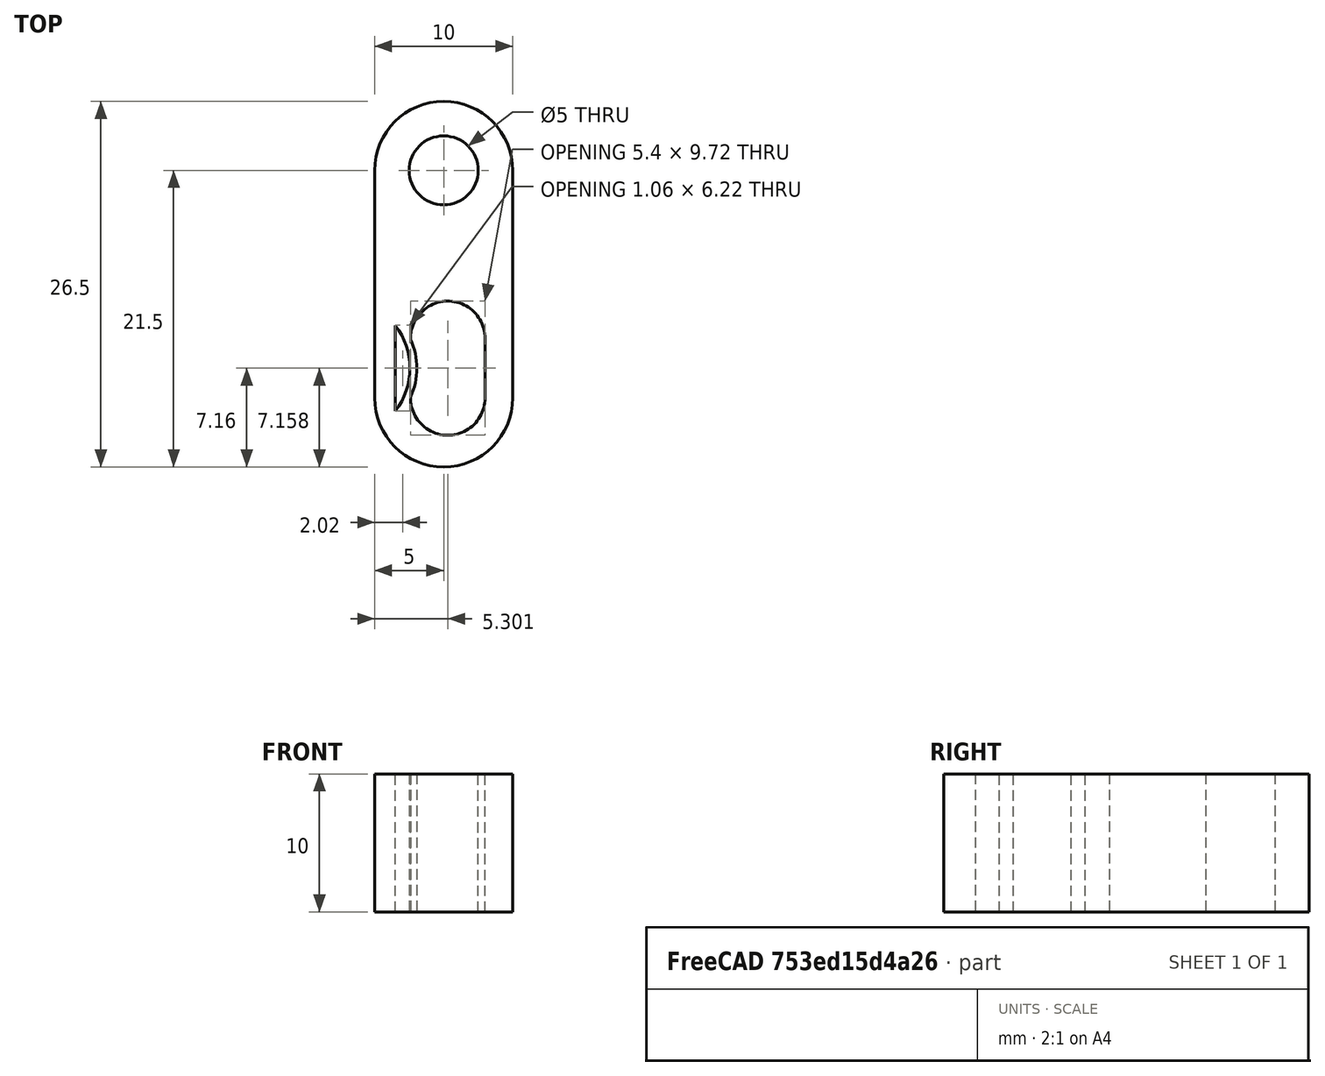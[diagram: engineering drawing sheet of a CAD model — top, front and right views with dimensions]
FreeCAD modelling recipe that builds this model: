
FCSTD DOCUMENT  (FreeCAD 0.22R38467 (Git))
Label: Actuator Arm
objects: Sketcher::SketchObject×2, PartDesign::CoordinateSystem×1, Part::Extrusion×1, App::Part×1
note: 6 computed .brp shape members not serialized (recipe doc carries the construction recipe); baked Part::Feature solids carry a one-line shape summary decoded from their .brp

FEATURE [Sketcher::SketchObject] Sketch001  label="Master Sketch"
  ArcFitTolerance = 1e-06
  FullyConstrained = false
  MakeInternals = false
  sketch-geometry (42):
    g0: Circle CenterX=-4e-16 CenterY=0 CenterZ=0 NormalX=0 NormalY=0 NormalZ=1 AngleXU=0 Radius=50
    g1: LineSegment [constr] StartX=-4e-16 StartY=0 StartZ=0 EndX=-15.4508 EndY=-47.5528 EndZ=0
    g2: LineSegment [constr] StartX=-4e-16 StartY=0 StartZ=0 EndX=15.4508 EndY=-47.5528 EndZ=0
    g3: LineSegment StartX=4.16347 StartY=-17.7687 StartZ=0 EndX=-5.80371 EndY=-32.7572 EndZ=0
    g4: LineSegment StartX=-6.93214 StartY=-16.3948 StartZ=0 EndX=-14.1307 EndY=-27.2198 EndZ=0
    g5: ArcOfCircle [constr] CenterX=1e-16 CenterY=-15 CenterZ=0 NormalX=0 NormalY=0 NormalZ=1 AngleXU=0 Radius=15 StartAngle=4.08407 EndAngle=5.34071
    g6: Circle CenterX=-9.04623 CenterY=-28.6036 CenterZ=0 NormalX=0 NormalY=0 NormalZ=1 AngleXU=0 Radius=2.5
    g7: Circle CenterX=1e-16 CenterY=-15 CenterZ=0 NormalX=0 NormalY=0 NormalZ=1 AngleXU=0 Radius=2.5
    g8: ArcOfCircle CenterX=-12.4904 CenterY=-6.69401 CenterZ=0 NormalX=0 NormalY=0 NormalZ=1 AngleXU=0 Radius=5 StartAngle=0.983956 EndAngle=4.12555
    g9: LineSegment StartX=-6.93214 StartY=-16.3948 StartZ=0 EndX=-15.2591 EndY=-10.8575 EndZ=0
    g10: LineSegment StartX=2.76866 StartY=-10.8365 StartZ=0 EndX=-9.72176 EndY=-2.53054 EndZ=0
    g11: ArcOfCircle CenterX=1e-16 CenterY=-15 CenterZ=0 NormalX=0 NormalY=0 NormalZ=1 AngleXU=0 Radius=5 StartAngle=5.69635 EndAngle=7.26714
    g12: ArcOfCircle CenterX=-9.96718 CenterY=-29.9885 CenterZ=0 NormalX=0 NormalY=0 NormalZ=1 AngleXU=0 Radius=5 StartAngle=2.55475 EndAngle=5.69635
    g13: ArcOfCircle CenterX=-9.96718 CenterY=-29.9885 CenterZ=0 NormalX=0 NormalY=0 NormalZ=1 AngleXU=0 Radius=2.7 StartAngle=2.55475 EndAngle=5.69635
    g14: ArcOfCircle CenterX=-8.30599 CenterY=-27.4904 CenterZ=0 NormalX=0 NormalY=0 NormalZ=1 AngleXU=0 Radius=2.7 StartAngle=5.69635 EndAngle=8.83794
    g15: LineSegment [constr] StartX=-12.2155 StartY=-28.4934 StartZ=0 EndX=-10.5543 EndY=-25.9953 EndZ=0
    g16: LineSegment StartX=-7.71891 StartY=-31.4836 StartZ=0 EndX=-6.05771 EndY=-28.9855 EndZ=0
    g17: LineSegment [constr] StartX=1e-16 StartY=-15 StartZ=0 EndX=-20.3856 EndY=-45.6555 EndZ=0
    g18: Circle CenterX=-12.4904 CenterY=-6.69401 CenterZ=0 NormalX=0 NormalY=0 NormalZ=1 AngleXU=0 Radius=2.5
    g19: ArcOfCircle CenterX=-4e-16 CenterY=0 CenterZ=0 NormalX=0 NormalY=0 NormalZ=1 AngleXU=0 Radius=27.6248 StartAngle=1.25664 EndAngle=1.88496
    g20: ArcOfCircle CenterX=-7.70217 CenterY=23.7048 CenterZ=0 NormalX=0 NormalY=0 NormalZ=1 AngleXU=0 Radius=2.7 StartAngle=1.88496 EndAngle=5.02655
    g21: ArcOfCircle CenterX=7.70217 CenterY=23.7048 CenterZ=0 NormalX=0 NormalY=0 NormalZ=1 AngleXU=0 Radius=2.7 StartAngle=4.39823 EndAngle=7.53982
    g22: ArcOfCircle CenterX=-4e-16 CenterY=0 CenterZ=0 NormalX=0 NormalY=0 NormalZ=1 AngleXU=0 Radius=22.2248 StartAngle=1.25664 EndAngle=1.88496
    g23: LineSegment [constr] StartX=-4e-16 StartY=0 StartZ=0 EndX=7.70217 EndY=23.7048 EndZ=0
    g24: LineSegment [constr] StartX=-4e-16 StartY=0 StartZ=0 EndX=-7.70217 EndY=23.7048 EndZ=0
    g25: Circle CenterX=-0.054258 CenterY=24.7641 CenterZ=0 NormalX=0 NormalY=0 NormalZ=1 AngleXU=0 Radius=2.5
    g26: ArcOfCircle CenterX=-15.3566 CenterY=-24.6032 CenterZ=0 NormalX=0 NormalY=0 NormalZ=1 AngleXU=0 Radius=5 StartAngle=5.39165 EndAngle=6.00104
    g27: ArcOfCircle CenterX=-15.3566 CenterY=-24.6032 CenterZ=0 NormalX=0 NormalY=0 NormalZ=1 AngleXU=0 Radius=4.39478 StartAngle=5.2351 EndAngle=6.15759
    g28: LineSegment [constr] StartX=-11.3849 StartY=-27.2444 StartZ=0 EndX=-13.3001 EndY=-25.9708 EndZ=0
    g29: LineSegment [constr] StartX=-13.3001 StartY=-25.9708 StartZ=0 EndX=-10.5543 EndY=-25.9953 EndZ=0
    g30: LineSegment [constr] StartX=-13.3001 StartY=-25.9708 StartZ=0 EndX=-12.2155 EndY=-28.4934 EndZ=0
    g31: LineSegment StartX=-10.9964 StartY=-25.1537 StartZ=0 EndX=-11.4964 EndY=-25.1493 EndZ=0
    g32: LineSegment StartX=-11.4964 StartY=-25.1493 StartZ=0 EndX=-13.3601 EndY=-27.9519 EndZ=0
    g33: LineSegment StartX=-13.3601 StartY=-27.9519 StartZ=0 EndX=-13.1626 EndY=-28.4112 EndZ=0
    g34: LineSegment [constr] StartX=-4e-16 StartY=0 StartZ=0 EndX=-75.0332 EndY=-40.2127 EndZ=0
    g35: LineSegment [constr] StartX=-17.7952 StartY=13.7094 StartZ=0 EndX=6.06492 EndY=-30.8114 EndZ=0
    g36: Circle CenterX=-4e-16 CenterY=0 CenterZ=0 NormalX=0 NormalY=0 NormalZ=1 AngleXU=0 Radius=11
    g37: Circle CenterX=-4e-16 CenterY=0 CenterZ=0 NormalX=0 NormalY=0 NormalZ=1 AngleXU=0 Radius=30
    g38: Circle [constr] CenterX=-6.1698 CenterY=-3.30659 CenterZ=0 NormalX=0 NormalY=0 NormalZ=1 AngleXU=0 Radius=11
    g39: Circle [constr] CenterX=4.407 CenterY=2.36185 CenterZ=0 NormalX=0 NormalY=0 NormalZ=1 AngleXU=0 Radius=30
    g40: LineSegment [constr] StartX=-13.8538 StartY=-26.8035 StartZ=0 EndX=-12.6421 EndY=-29.6216 EndZ=0
    g41: LineSegment [constr] StartX=-12.7463 StartY=-25.1381 StartZ=0 EndX=-9.67889 EndY=-25.1655 EndZ=0
  constraints (104):
    c: Diameter(g0) = 100
    c: Coincident(g0,g-1)
    c: Coincident(g1,g0)
    c: PointOnObject(g1,g0)
    c: Coincident(g2,g0)
    c: Symmetric(g2,g1,g-2)
    c: Angle(g1,g2) = 0.628319
    c: PointOnObject(g5,g1)
    c: PointOnObject(g5,g2)
    c: Diameter(g6) = 5
    c: Equal(g7,g6)
    c: Tangent(g8,g9) = 1.5708
    c: Tangent(g8,g10) = -1.5708
    c: Coincident(g9,g4)
    c: Parallel(g3,g4)
    c: Parallel(g9,g10)
    c: Coincident(g11,g7)
    c: Tangent(g11,g3) = 1.5708
    c: Tangent(g11,g10) = -1.5708
    c: Coincident(g7,g5)
    c: PointOnObject(g5,g-2)
    c: DistanceY(g5,g0) = 15
    c: Perpendicular(g9,g4)
    c: Equal(g11,g8)
    c: Radius(g5) = 15
    c: Equal(g12,g8)
    c: Tangent(g12,g3) = 1.5708
    c: Tangent(g12,g4) = -1.5708
    c: Radius(g8) = 5
    c: Distance(g8,g5) = 15
    c: Tangent(g13,g15) = 1.5708
    c: Tangent(g13,g16) = -1.5708
    c: Tangent(g14,g15) = 1.5708
    c: Tangent(g14,g16) = -1.5708
    c: Equal(g13,g14)
    c: Distance(g13,g14) = 3
    c: Radius(g14) = 2.7
    c: Coincident(g17,g5)
    c: PointOnObject(g17,g0)
    c: PointOnObject(g13,g17)
    c: Distance(g14,g5) = 15
    c: PointOnObject(g14,g17)
    c: Coincident(g13,g12)
    c: Distance(g6,g0) = 30
    c: PointOnObject(g6,g17)
    c: Diameter(g18) = 5
    c: Coincident(g18,g8)
    c: Coincident(g19,g22)
    c: Tangent(g22,g21) = 1.5708
    c: Tangent(g22,g20) = 1.5708
    c: Tangent(g19,g21) = -1.5708
    c: Tangent(g19,g20) = -1.5708
    c: Coincident(g19,g0)
    c: Coincident(g23,g0)
    c: Coincident(g23,g21)
    c: Coincident(g24,g0)
    c: Coincident(g24,g20)
    c: Angle(g23,g24) = 0.628319
    c: Distance(g20,g19) = 5.4
    c: Angle(g23,g-2) = 0.314159
    c: Diameter(g25) = 5
    c: Coincident(g26,g14)
    c: Coincident(g26,g13)
    c: Coincident(g27,g26)
    c: Symmetric(g15,g15,g28)
    c: Perpendicular(g15,g28)
    c: Coincident(g29,g14)
    c: Coincident(g30,g29)
    c: Coincident(g30,g13)
    c: Coincident(g27,g31)
    c: Coincident(g31,g32)
    c: Coincident(g32,g33)
    c: Coincident(g33,g27)
    c: Distance(g31) = 0.5
    c: Coincident(g28,g29)
    c: PointOnObject(g28,g4)
    c: Radius(g26) = 5
    c: Equal(g33,g31)
    c: Coincident(g34,g0)
    c: PointOnObject(g8,g34)
    c: Perpendicular(g34,g35)
    c: Diameter(g36) = 22
    c: Coincident(g36,g0)
    c: Diameter(g37) = 60
    c: Coincident(g37,g0)
    c: PointOnObject(g38,g34)
    c: Distance(g38,g0) = 7
    c: PointOnObject(g39,g34)
    c: Distance(g39,g0) = 5
    c: Equal(g39,g37)
    c: Equal(g38,g36)
    c: PointOnObject(g40,g4)
    c: PointOnObject(g40,g13)
    c: PointOnObject(g41,g4)
    c: PointOnObject(g41,g14)
    c: Parallel(g41,g29)
    c: Parallel(g30,g40)
    c: Distance(g40,g28) = 1
    c: Distance(g41,g28) = 1
    c: PointOnObject(g31,g41)
    c: PointOnObject(g32,g40)
    c: PointOnObject(g27,g40)
    c: PointOnObject(g27,g41)
    c: Distance(g41,g31) = 1.25
FEATURE [Sketcher::SketchObject] Sketch
  ArcFitTolerance = 1e-06
  FullyConstrained = false
  MakeInternals = false
  sketch-geometry (11):
    g0: Circle CenterX=0 CenterY=0 CenterZ=0 NormalX=0 NormalY=0 NormalZ=1 AngleXU=0 Radius=2.5
    g1: ArcOfCircle CenterX=0 CenterY=0 CenterZ=0 NormalX=0 NormalY=0 NormalZ=1 AngleXU=0 Radius=5 StartAngle=1e-16 EndAngle=3.14159
    g2: ArcOfCircle CenterX=2e-16 CenterY=-16.5 CenterZ=0 NormalX=0 NormalY=0 NormalZ=1 AngleXU=0 Radius=5 StartAngle=3.14159 EndAngle=6.28319
    g3: LineSegment StartX=5 StartY=6e-16 StartZ=0 EndX=5 EndY=-16.5 EndZ=0
    g4: LineSegment StartX=-5 StartY=6e-16 StartZ=0 EndX=-5 EndY=-16.5 EndZ=0
    g5: ArcOfCircle CenterX=0.300118 CenterY=-16.5 CenterZ=0 NormalX=0 NormalY=0 NormalZ=1 AngleXU=0 Radius=2.7 StartAngle=3.1166 EndAngle=6.28319
    g6: ArcOfCircle CenterX=0.300118 CenterY=-12.1792 CenterZ=0 NormalX=0 NormalY=0 NormalZ=1 AngleXU=0 Radius=2.7 StartAngle=3e-16 EndAngle=3.16849
    g7: LineSegment StartX=3.00012 StartY=-16.5 StartZ=0 EndX=3.00012 EndY=-12.1792 EndZ=0
    g8: ArcOfCircle CenterX=-7.03445 CenterY=-14.342 CenterZ=0 NormalX=0 NormalY=0 NormalZ=1 AngleXU=0 Radius=5.085 StartAngle=5.85951 EndAngle=6.70679
    g9: ArcOfCircle CenterX=-7.53445 CenterY=-14.342 CenterZ=0 NormalX=0 NormalY=0 NormalZ=1 AngleXU=0 Radius=5.085 StartAngle=5.62544 EndAngle=6.94093
    g10: LineSegment StartX=-3.51031 StartY=-11.2334 StartZ=0 EndX=-3.51031 EndY=-17.4506 EndZ=0
  constraints (25):
    c: Diameter(g0) = 5
    c: Coincident(g0,g-1)
    c: Tangent(g1,g3) = 1.5708
    c: Tangent(g1,g4) = -1.5708
    c: Tangent(g2,g3) = 1.5708
    c: Tangent(g2,g4) = -1.5708
    c: Equal(g1,g2)
    c: Vertical(g4)
    c: Coincident(g1,g0)
    c: DistanceY(g3,g3) = 16.5
    c: Radius(g2) = 5
    c: Tangent(g5,g7) = -1.5708
    c: Tangent(g6,g7) = -1.5708
    c: Equal(g5,g6)
    c: Vertical(g7)
    c: Radius(g6) = 2.7
    c: Horizontal(g2,g5)
    c: Coincident(g8,g6)
    c: Coincident(g8,g5)
    c: Equal(g9,g8)
    c: Horizontal(g9,g8)
    c: DistanceX(g9,g8) = 0.5
    c: Coincident(g10,g9)
    c: Coincident(g10,g9)
    c: Vertical(g10)
FEATURE [PartDesign::CoordinateSystem] LCS_Origin
  AttacherType = Attacher::AttachEngine3D
  AttachmentSupport = -> [X_Axis]
  MapMode = 2
FEATURE [Part::Extrusion] Extrude
  Base = -> Sketch
  Dir = (0,0,1)
  DirMode = 2
  FaceMakerClass = Part::FaceMakerBullseye
  FaceMakerMode = 3
  LengthFwd = 10
  LengthRev = 0
  Solid = true
  Symmetric = false
FEATURE [App::Part] Actuator_Arm  label="Actuator Arm"
  Group = -> [LCS_Origin,Sketch,Extrude]
  Origin = -> Origin
